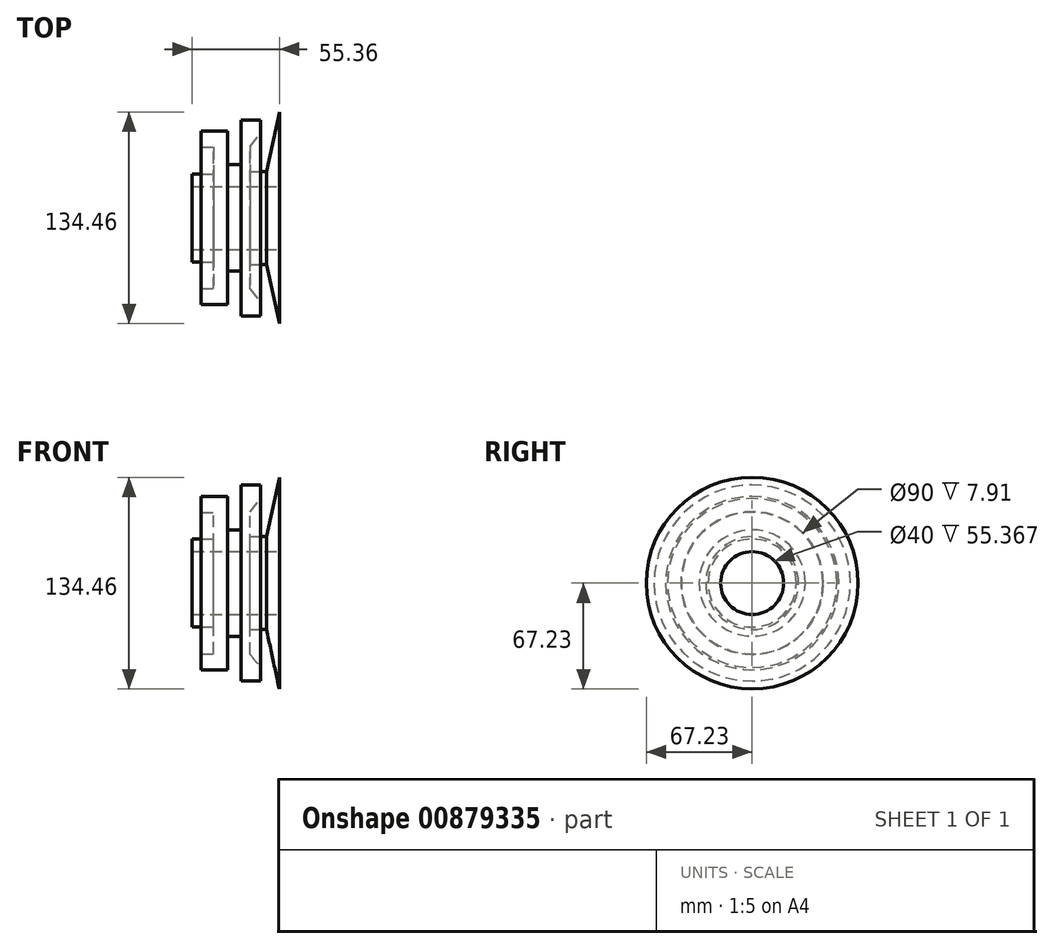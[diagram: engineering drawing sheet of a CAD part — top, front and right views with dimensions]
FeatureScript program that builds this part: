
annotation { "Feature Type Name" : "Feature", "Feature Type Description" : "" }
export const myFeature = defineFeature(function(context is Context, id is Id, definition is map)
    precondition{}
    {
        {
            var Q0;
            Q0=qCreatedBy(makeId("Front.planeOp"),FACE);
            var sketch = newSketch(context, id + "F0", { "sketchPlane" : qUnion([Q0])});
            skLineSegment(sketch, "E0", {"start": v(24.3, 67.23) * mm, "end": v(24.3, 20) * mm});
            skLineSegment(sketch, "E1", {"start": v(24.3, 20) * mm, "end": v(-31.07, 20) * mm});
            skLineSegment(sketch, "E2", {"start": v(-31.07, 20) * mm, "end": v(-31.07, 28) * mm});
            skLineSegment(sketch, "E3", {"start": v(-31.07, 28) * mm, "end": v(-17.51, 28) * mm});
            skLineSegment(sketch, "E4", {"start": v(-17.51, 28) * mm, "end": v(-17.51, 45) * mm});
            skLineSegment(sketch, "E5", {"start": v(-17.51, 45) * mm, "end": v(-25.42, 45) * mm});
            skLineSegment(sketch, "E6", {"start": v(-25.42, 45) * mm, "end": v(-25.42, 55) * mm});
            skLineSegment(sketch, "E7", {"start": v(-25.42, 55) * mm, "end": v(-8.47, 55) * mm});
            skLineSegment(sketch, "E8", {"start": v(-8.47, 55) * mm, "end": v(-8.47, 33.76) * mm});
            skLineSegment(sketch, "E9", {"start": v(-8.47, 33.76) * mm, "end": v(0, 33.76) * mm});
            skLineSegment(sketch, "E10", {"start": v(0, 33.76) * mm, "end": v(0, 62.26) * mm});
            skLineSegment(sketch, "E11", {"start": v(0, 62.26) * mm, "end": v(12.32, 62.26) * mm});
            skLineSegment(sketch, "E12", {"start": v(12.32, 62.26) * mm, "end": v(12.32, 53.67) * mm});
            skLineSegment(sketch, "E13", {"start": v(12.32, 53.67) * mm, "end": v(5.76, 45.31) * mm});
            skLineSegment(sketch, "E14", {"start": v(5.76, 45.31) * mm, "end": v(5.76, 29.5) * mm});
            skLineSegment(sketch, "E15", {"start": v(5.76, 29.5) * mm, "end": v(16.16, 29.5) * mm});
            skLineSegment(sketch, "E16", {"start": v(16.16, 29.5) * mm, "end": v(24.3, 67.23) * mm});
            skLineSegment(sketch, "E17", {"start": v(0, 0) * mm, "end": v(-82.37, 0) * mm, "construction": true});
            skSolve(sketch);
        }
        {
            var Q0;
            Q0 = qSketchRegion(id + "F0", true);
            var Q1;
            Q1=sQuery(id+"F0.wireOp",EDGE,"E17");
            revolve(context, id + "F1", {"surfaceOperationType" : NewSurfaceOperationType.NEW, "entities" : qUnion([Q0]), "axis" : qUnion([Q1]), "revolveType" : RevolveType.FULL});
        }
    });
